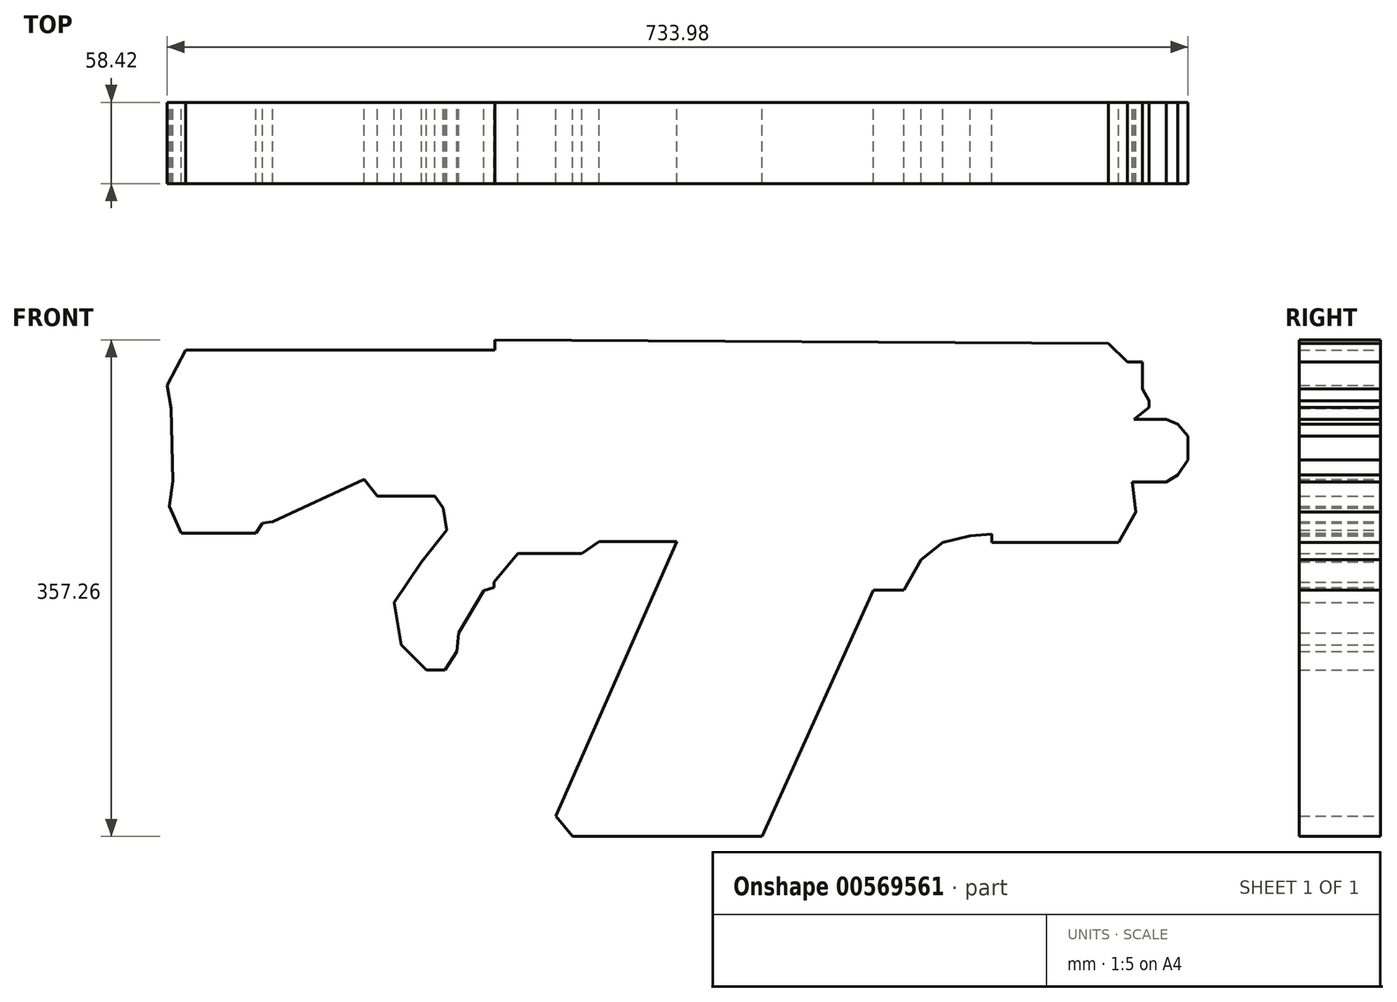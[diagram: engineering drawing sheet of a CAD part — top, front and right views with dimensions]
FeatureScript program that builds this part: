
annotation { "Feature Type Name" : "Feature", "Feature Type Description" : "" }
export const myFeature = defineFeature(function(context is Context, id is Id, definition is map)
    precondition{}
    {
        {
            var Q0;
            Q0=qCreatedBy(makeId("Front.planeOp"),FACE);
            var sketch = newSketch(context, id + "F0", { "sketchPlane" : qUnion([Q0])});
            skLineSegment(sketch, "E0", {"start": v(-366.99, 145.82) * mm, "end": v(-353.62, 171.34) * mm});
            skLineSegment(sketch, "E1", {"start": v(-353.62, 171.34) * mm, "end": v(-131.24, 171.34) * mm});
            skLineSegment(sketch, "E2", {"start": v(-131.24, 171.34) * mm, "end": v(-131.24, 178.63) * mm});
            skLineSegment(sketch, "E3", {"start": v(-131.24, 178.63) * mm, "end": v(309.87, 176.2) * mm});
            skLineSegment(sketch, "E4", {"start": v(309.87, 176.2) * mm, "end": v(323.24, 162.84) * mm});
            skLineSegment(sketch, "E5", {"start": v(323.24, 162.84) * mm, "end": v(334.18, 162.84) * mm});
            skLineSegment(sketch, "E6", {"start": v(334.18, 162.84) * mm, "end": v(334.18, 143.4) * mm});
            skLineSegment(sketch, "E7", {"start": v(334.18, 143.4) * mm, "end": v(339.04, 134.89) * mm});
            skLineSegment(sketch, "E8", {"start": v(339.04, 134.89) * mm, "end": v(339.04, 130.03) * mm});
            skLineSegment(sketch, "E9", {"start": v(339.04, 130.03) * mm, "end": v(328.1, 121.52) * mm});
            skLineSegment(sketch, "E10", {"start": v(328.1, 121.52) * mm, "end": v(351.19, 121.52) * mm});
            skLineSegment(sketch, "E11", {"start": v(351.19, 121.52) * mm, "end": v(359.7, 117.87) * mm});
            skLineSegment(sketch, "E12", {"start": v(359.7, 117.87) * mm, "end": v(366.99, 109.37) * mm});
            skLineSegment(sketch, "E13", {"start": v(366.99, 109.37) * mm, "end": v(366.99, 92.35) * mm});
            skLineSegment(sketch, "E14", {"start": v(366.99, 92.35) * mm, "end": v(359.7, 81.42) * mm});
            skLineSegment(sketch, "E15", {"start": v(359.7, 81.42) * mm, "end": v(351.19, 76.56) * mm});
            skLineSegment(sketch, "E16", {"start": v(351.19, 76.56) * mm, "end": v(326.89, 76.56) * mm});
            skLineSegment(sketch, "E17", {"start": v(326.89, 76.56) * mm, "end": v(329.32, 54.68) * mm});
            skLineSegment(sketch, "E18", {"start": v(329.32, 54.68) * mm, "end": v(317.16, 32.81) * mm});
            skLineSegment(sketch, "E19", {"start": v(317.16, 32.81) * mm, "end": v(226.03, 32.81) * mm});
            skLineSegment(sketch, "E20", {"start": v(226.03, 32.81) * mm, "end": v(226.03, 38.89) * mm});
            skLineSegment(sketch, "E21", {"start": v(226.03, 38.89) * mm, "end": v(210.23, 37.67) * mm});
            skLineSegment(sketch, "E22", {"start": v(210.23, 37.67) * mm, "end": v(190.78, 32.81) * mm});
            skLineSegment(sketch, "E23", {"start": v(190.78, 32.81) * mm, "end": v(174.99, 20.66) * mm});
            skLineSegment(sketch, "E24", {"start": v(174.99, 20.66) * mm, "end": v(162.84, -1.22) * mm});
            skLineSegment(sketch, "E25", {"start": v(162.84, -1.22) * mm, "end": v(140.96, -1.22) * mm});
            skLineSegment(sketch, "E26", {"start": v(140.96, -1.22) * mm, "end": v(60.76, -178.63) * mm});
            skLineSegment(sketch, "E27", {"start": v(60.76, -178.63) * mm, "end": v(-75.34, -178.63) * mm});
            skLineSegment(sketch, "E28", {"start": v(-75.34, -178.63) * mm, "end": v(-87.5, -164.05) * mm});
            skLineSegment(sketch, "E29", {"start": v(-87.5, -164.05) * mm, "end": v(-0.6, 33.42) * mm});
            skLineSegment(sketch, "E30", {"start": v(-0.6, 33.42) * mm, "end": v(-56.5, 33.42) * mm});
            skLineSegment(sketch, "E31", {"start": v(-56.5, 33.42) * mm, "end": v(-68.66, 24.91) * mm});
            skLineSegment(sketch, "E32", {"start": v(-68.66, 24.91) * mm, "end": v(-114.84, 24.91) * mm});
            skLineSegment(sketch, "E33", {"start": v(-114.84, 24.91) * mm, "end": v(-131.85, 4.25) * mm});
            skLineSegment(sketch, "E34", {"start": v(-131.85, 4.25) * mm, "end": v(-131.85, 0.6) * mm});
            skLineSegment(sketch, "E35", {"start": v(-131.85, 0.6) * mm, "end": v(-139.14, -1.82) * mm});
            skLineSegment(sketch, "E36", {"start": v(-139.14, -1.82) * mm, "end": v(-157.37, -32.2) * mm});
            skLineSegment(sketch, "E37", {"start": v(-157.37, -32.2) * mm, "end": v(-158.58, -45.57) * mm});
            skLineSegment(sketch, "E38", {"start": v(-158.58, -45.57) * mm, "end": v(-167.09, -58.94) * mm});
            skLineSegment(sketch, "E39", {"start": v(-167.09, -58.94) * mm, "end": v(-180.46, -58.94) * mm});
            skLineSegment(sketch, "E40", {"start": v(-180.46, -58.94) * mm, "end": v(-198.68, -40.7) * mm});
            skLineSegment(sketch, "E41", {"start": v(-198.68, -40.7) * mm, "end": v(-203.54, -10.33) * mm});
            skLineSegment(sketch, "E42", {"start": v(-203.54, -10.33) * mm, "end": v(-184.1, 18.84) * mm});
            skLineSegment(sketch, "E43", {"start": v(-184.1, 18.84) * mm, "end": v(-165.87, 41.92) * mm});
            skLineSegment(sketch, "E44", {"start": v(-165.87, 41.92) * mm, "end": v(-168.3, 57.72) * mm});
            skLineSegment(sketch, "E45", {"start": v(-168.3, 57.72) * mm, "end": v(-174.38, 66.23) * mm});
            skLineSegment(sketch, "E46", {"start": v(-174.38, 66.23) * mm, "end": v(-215.7, 66.23) * mm});
            skLineSegment(sketch, "E47", {"start": v(-215.7, 66.23) * mm, "end": v(-225.42, 78.38) * mm});
            skLineSegment(sketch, "E48", {"start": v(-225.42, 78.38) * mm, "end": v(-291.04, 48) * mm});
            skLineSegment(sketch, "E49", {"start": v(-291.04, 48) * mm, "end": v(-298.33, 46.78) * mm});
            skLineSegment(sketch, "E50", {"start": v(-298.33, 46.78) * mm, "end": v(-303.19, 39.5) * mm});
            skLineSegment(sketch, "E51", {"start": v(-303.19, 39.5) * mm, "end": v(-356.66, 39.5) * mm});
            skLineSegment(sketch, "E52", {"start": v(-356.66, 39.5) * mm, "end": v(-365.16, 58.94) * mm});
            skLineSegment(sketch, "E53", {"start": v(-365.16, 58.94) * mm, "end": v(-362.73, 77.16) * mm});
            skLineSegment(sketch, "E54", {"start": v(-362.73, 77.16) * mm, "end": v(-363.95, 129.42) * mm});
            skLineSegment(sketch, "E55", {"start": v(-363.95, 129.42) * mm, "end": v(-366.99, 145.82) * mm});
            skSolve(sketch);
        }
        {
            var Q0;
            Q0=makeQuery(id+"F0.imprint","IMPRINT",FACE,{"disambiguationData":[TD([[makeQuery(id+"F0.imprint","IMPRINT",EDGE,{"derivedFrom":sQuery(id+"F0.wireOp",EDGE,"E0")}),-1.0]])]});
            extrude(context, id + "F1", {"entities" : qUnion([Q0]), "depth" : 58.42 * mm, "offsetDistance" : 25.4 * mm});
        }
    });
